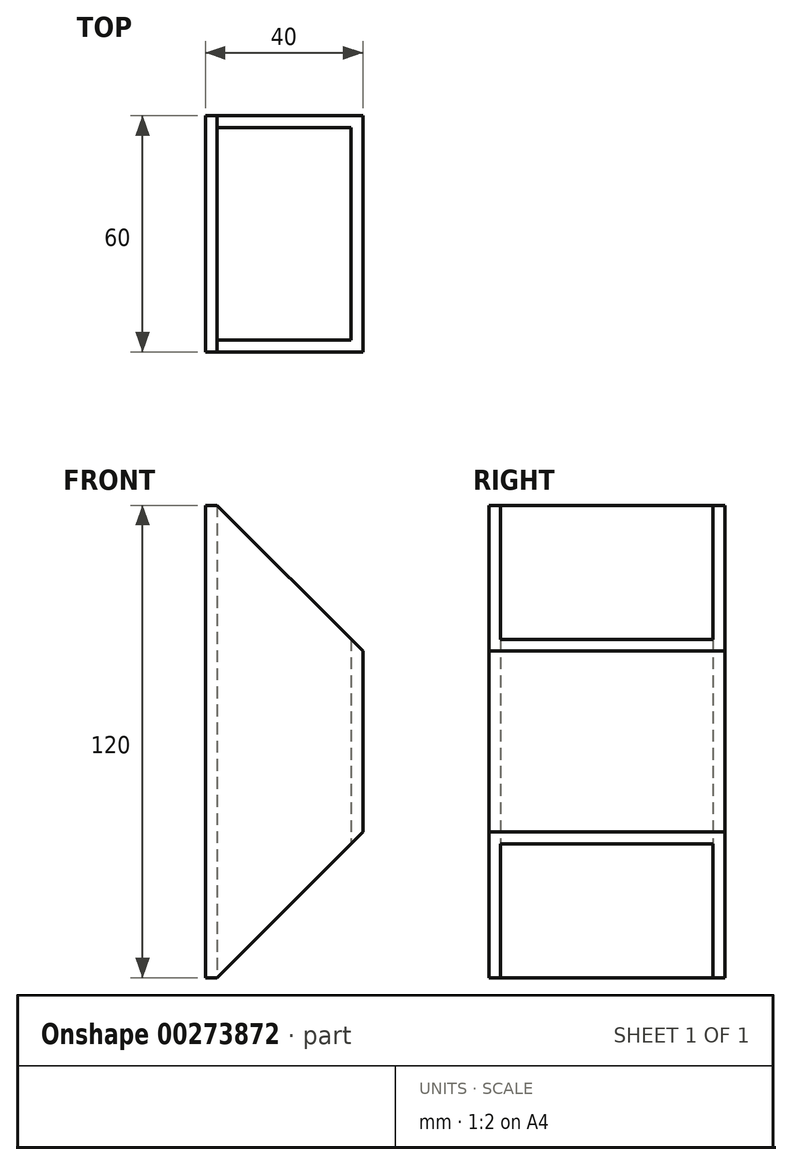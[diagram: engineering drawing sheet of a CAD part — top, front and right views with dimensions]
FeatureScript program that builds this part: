
annotation { "Feature Type Name" : "Feature", "Feature Type Description" : "" }
export const myFeature = defineFeature(function(context is Context, id is Id, definition is map)
    precondition{}
    {
        {
            var Q0;
            Q0=qCreatedBy(makeId("Front.planeOp"),FACE);
            var sketch = newSketch(context, id + "F0", { "sketchPlane" : qUnion([Q0])});
            skLineSegment(sketch, "E0.bottom", {"start": v(20, 60) * mm, "end": v(-20, 60) * mm});
            skLineSegment(sketch, "E0.top", {"start": v(20, -60) * mm, "end": v(-20, -60) * mm});
            skLineSegment(sketch, "E0.left", {"start": v(20, 60) * mm, "end": v(20, -60) * mm});
            skLineSegment(sketch, "E0.right", {"start": v(-20, 60) * mm, "end": v(-20, -60) * mm});
            skPoint(sketch, "E0.middle", {"position": v(0, 0) * mm});
            skSolve(sketch);
        }
        {
            var Q0;
            Q0=qSketchRegion(id+"F0",true);
            extrude(context, id + "F1", {"entities" : qUnion([Q0]), "depth" : 60 * mm});
        }
        {
            var Q0;
            Q0=makeQuery(id+"F1.opExtrude","SWEPT_FACE",FACE,{"disambiguationData":[OSD([sQuery(id+"F0.wireOp",EDGE,"E0.top")])]});
            var sketch = newSketch(context, id + "F2", { "sketchPlane" : qUnion([Q0])});
            skLineSegment(sketch, "E1.bottom", {"start": v(17, 3) * mm, "end": v(-17, 3) * mm});
            skLineSegment(sketch, "E1.top", {"start": v(17, 57) * mm, "end": v(-17, 57) * mm});
            skLineSegment(sketch, "E1.left", {"start": v(17, 3) * mm, "end": v(17, 57) * mm});
            skLineSegment(sketch, "E1.right", {"start": v(-17, 3) * mm, "end": v(-17, 57) * mm});
            skPoint(sketch, "E1.middle", {"position": v(0, 30) * mm});
            skPoint(sketch, "E1.middle.positionSnap0", {"position": v(20, 30) * mm});
            skPoint(sketch, "E1.centerSnap0", {"position": v(20, 30) * mm});
            skSolve(sketch);
        }
        {
            var Q0;
            Q0=makeQuery(id+"F2.imprint","IMPRINT",FACE,{"disambiguationData":[TD([[makeQuery(id+"F2.imprint","IMPRINT",EDGE,{"derivedFrom":sQuery(id+"F2.wireOp",EDGE,"E1.bottom")}),-1.0]])]});
            extrude(context, id + "F3", {"entities" : qUnion([Q0]), "operationType" : NewBodyOperationType.REMOVE, "oppositeDirection" : true, "depth" : 450 * mm});
        }
        {
            var Q0;
            Q0=makeQuery(id+"F1.opExtrude","CAP_FACE",FACE,{"disambiguationData":[OSD([sQuery(id+"F0.wireOp",EDGE,"E0.bottom"),sQuery(id+"F0.wireOp",EDGE,"E0.top"),sQuery(id+"F0.wireOp",EDGE,"E0.left"),sQuery(id+"F0.wireOp",EDGE,"E0.right")])],"isStart":false});
            var sketch = newSketch(context, id + "F4", { "sketchPlane" : qUnion([Q0])});
            skPoint(sketch, "E2", {"position": v(-17, 60) * mm});
            skPoint(sketch, "E3", {"position": v(20, 23) * mm});
            skPoint(sketch, "E4", {"position": v(20, -23) * mm});
            skPoint(sketch, "E5", {"position": v(-17, -60) * mm});
            skLineSegment(sketch, "E6", {"start": v(-17, 60) * mm, "end": v(20, 23) * mm});
            skLineSegment(sketch, "E7", {"start": v(20, 60) * mm, "end": v(20, 23) * mm});
            skLineSegment(sketch, "E8", {"start": v(-17, 60) * mm, "end": v(20, 60) * mm});
            skLineSegment(sketch, "E9", {"start": v(20, -23) * mm, "end": v(-17, -60) * mm});
            skLineSegment(sketch, "E10", {"start": v(20, -23) * mm, "end": v(20, -60) * mm});
            skLineSegment(sketch, "E11", {"start": v(-17, -60) * mm, "end": v(20, -60) * mm});
            skSolve(sketch);
        }
        {
            var Q0;
            Q0=makeQuery(id+"F4.imprint","IMPRINT",FACE,{"disambiguationData":[TD([[makeQuery(id+"F4.imprint","IMPRINT",EDGE,{"derivedFrom":sQuery(id+"F4.wireOp",EDGE,"E6")}),1.0]])]});
            var Q1;
            Q1=makeQuery(id+"F4.imprint","IMPRINT",FACE,{"disambiguationData":[TD([[makeQuery(id+"F4.imprint","IMPRINT",EDGE,{"derivedFrom":sQuery(id+"F4.wireOp",EDGE,"E9")}),1.0]])]});
            extrude(context, id + "F5", {"entities" : qUnion([Q0, Q1]), "operationType" : NewBodyOperationType.REMOVE, "oppositeDirection" : true, "depth" : 61 * mm});
        }
    });
